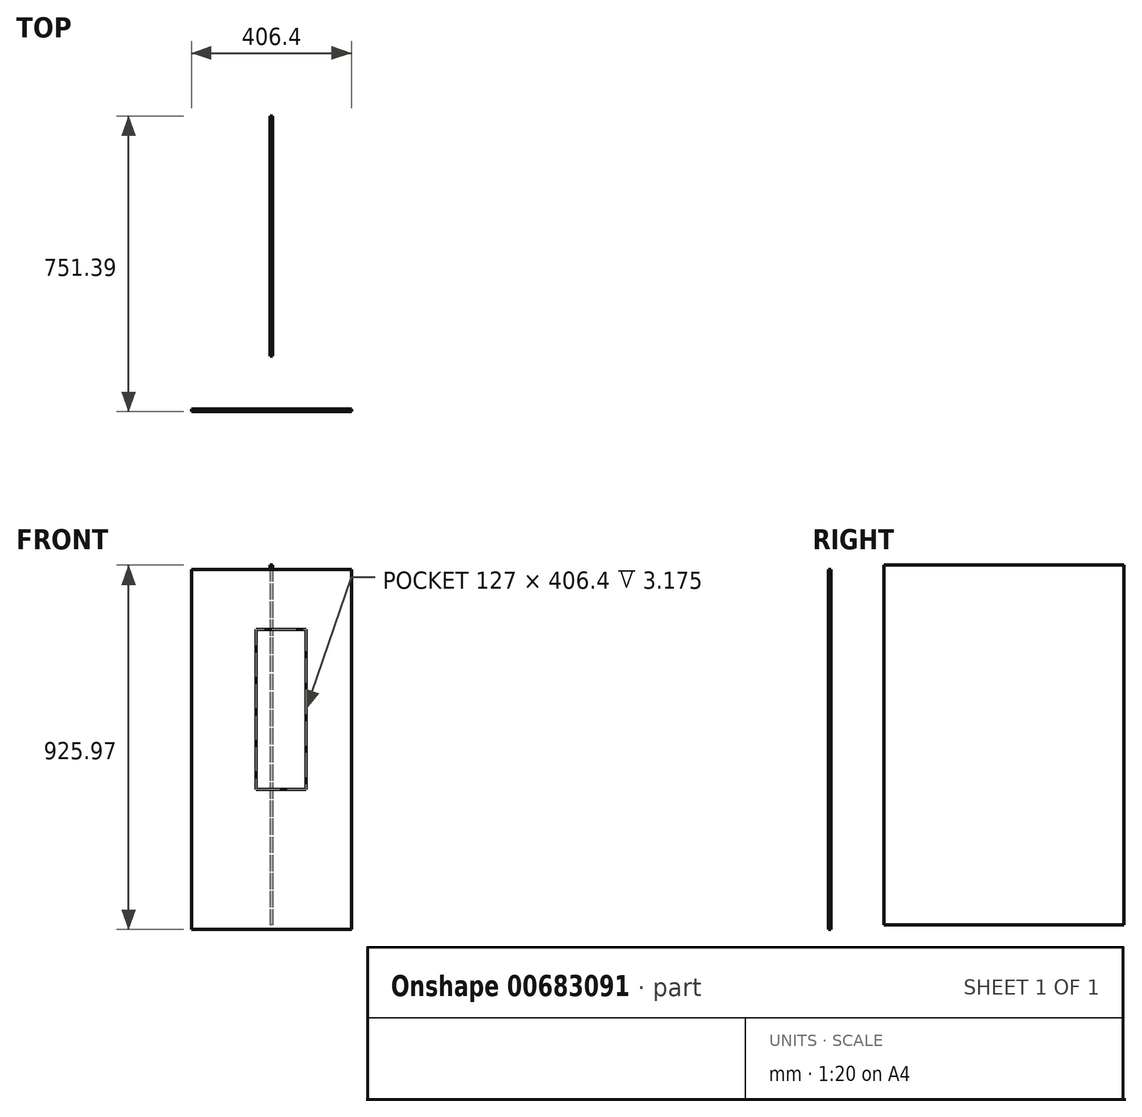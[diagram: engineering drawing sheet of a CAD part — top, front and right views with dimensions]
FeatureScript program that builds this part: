
annotation { "Feature Type Name" : "Feature", "Feature Type Description" : "" }
export const myFeature = defineFeature(function(context is Context, id is Id, definition is map)
    precondition{}
    {
        {
            var Q0;
            Q0=qCreatedBy(makeId("Front.planeOp"),FACE);
            var sketch = newSketch(context, id + "F0", { "sketchPlane" : qUnion([Q0])});
            skLineSegment(sketch, "E0.bottom", {"start": v(-203.2, 457.2) * mm, "end": v(203.2, 457.2) * mm});
            skLineSegment(sketch, "E0.top", {"start": v(-203.2, -457.2) * mm, "end": v(203.2, -457.2) * mm});
            skLineSegment(sketch, "E0.left", {"start": v(-203.2, 457.2) * mm, "end": v(-203.2, -457.2) * mm});
            skLineSegment(sketch, "E0.right", {"start": v(203.2, 457.2) * mm, "end": v(203.2, -457.2) * mm});
            skPoint(sketch, "E0.middle", {"position": v(0, 0) * mm});
            skSolve(sketch);
        }
        {
            var Q0;
            Q0=makeQuery(id+"F0.imprint","IMPRINT",FACE,{"disambiguationData":[TD([[makeQuery(id+"F0.imprint","IMPRINT",EDGE,{"derivedFrom":sQuery(id+"F0.wireOp",EDGE,"E0.bottom")}),-1.0]])]});
            var sketch = newSketch(context, id + "F1", { "sketchPlane" : qUnion([Q0])});
            skLineSegment(sketch, "E1.bottom", {"start": v(-39.3, 304.8) * mm, "end": v(87.7, 304.8) * mm});
            skLineSegment(sketch, "E1.top", {"start": v(-39.3, -101.6) * mm, "end": v(87.7, -101.6) * mm});
            skLineSegment(sketch, "E1.left", {"start": v(-39.3, 304.8) * mm, "end": v(-39.3, -101.6) * mm});
            skLineSegment(sketch, "E1.right", {"start": v(87.7, 304.8) * mm, "end": v(87.7, -101.6) * mm});
            skSolve(sketch);
        }
        {
            var Q0;
            Q0=makeQuery(id+"F0.imprint","IMPRINT",FACE,{"disambiguationData":[TD([[makeQuery(id+"F0.imprint","IMPRINT",EDGE,{"derivedFrom":sQuery(id+"F0.wireOp",EDGE,"E0.bottom")}),-1.0]])]});
            extrude(context, id + "F2", {"entities" : qUnion([Q0]), "endBound" : BoundingType.SYMMETRIC, "depth" : 6.35 * mm, "offsetDistance" : 25.4 * mm});
        }
        {
            var Q0;
            Q0=qCreatedBy(makeId("Right.planeOp"),FACE);
            var sketch = newSketch(context, id + "F3", { "sketchPlane" : qUnion([Q0])});
            skLineSegment(sketch, "E2.bottom", {"start": v(138.62, 468.77) * mm, "end": v(748.22, 468.77) * mm});
            skLineSegment(sketch, "E2.top", {"start": v(138.62, -445.63) * mm, "end": v(748.22, -445.63) * mm});
            skLineSegment(sketch, "E2.left", {"start": v(138.62, 468.77) * mm, "end": v(138.62, -445.63) * mm});
            skLineSegment(sketch, "E2.right", {"start": v(748.22, 468.77) * mm, "end": v(748.22, -445.63) * mm});
            skSolve(sketch);
        }
        {
            var Q0;
            Q0=makeQuery(id+"F3.imprint","IMPRINT",FACE,{"disambiguationData":[TD([[makeQuery(id+"F3.imprint","IMPRINT",EDGE,{"derivedFrom":sQuery(id+"F3.wireOp",EDGE,"E2.bottom")}),-1.0]])]});
            extrude(context, id + "F4", {"entities" : qUnion([Q0]), "endBound" : BoundingType.SYMMETRIC, "depth" : 6.35 * mm, "offsetDistance" : 25.4 * mm});
        }
        {
            var Q0;
            Q0 = qSketchRegion(id + "F1", true);
            extrude(context, id + "F5", {"entities" : qUnion([Q0]), "operationType" : NewBodyOperationType.REMOVE, "endBound" : BoundingType.THROUGH_ALL, "depth" : 25.4 * mm, "offsetDistance" : 25.4 * mm});
        }
    });
